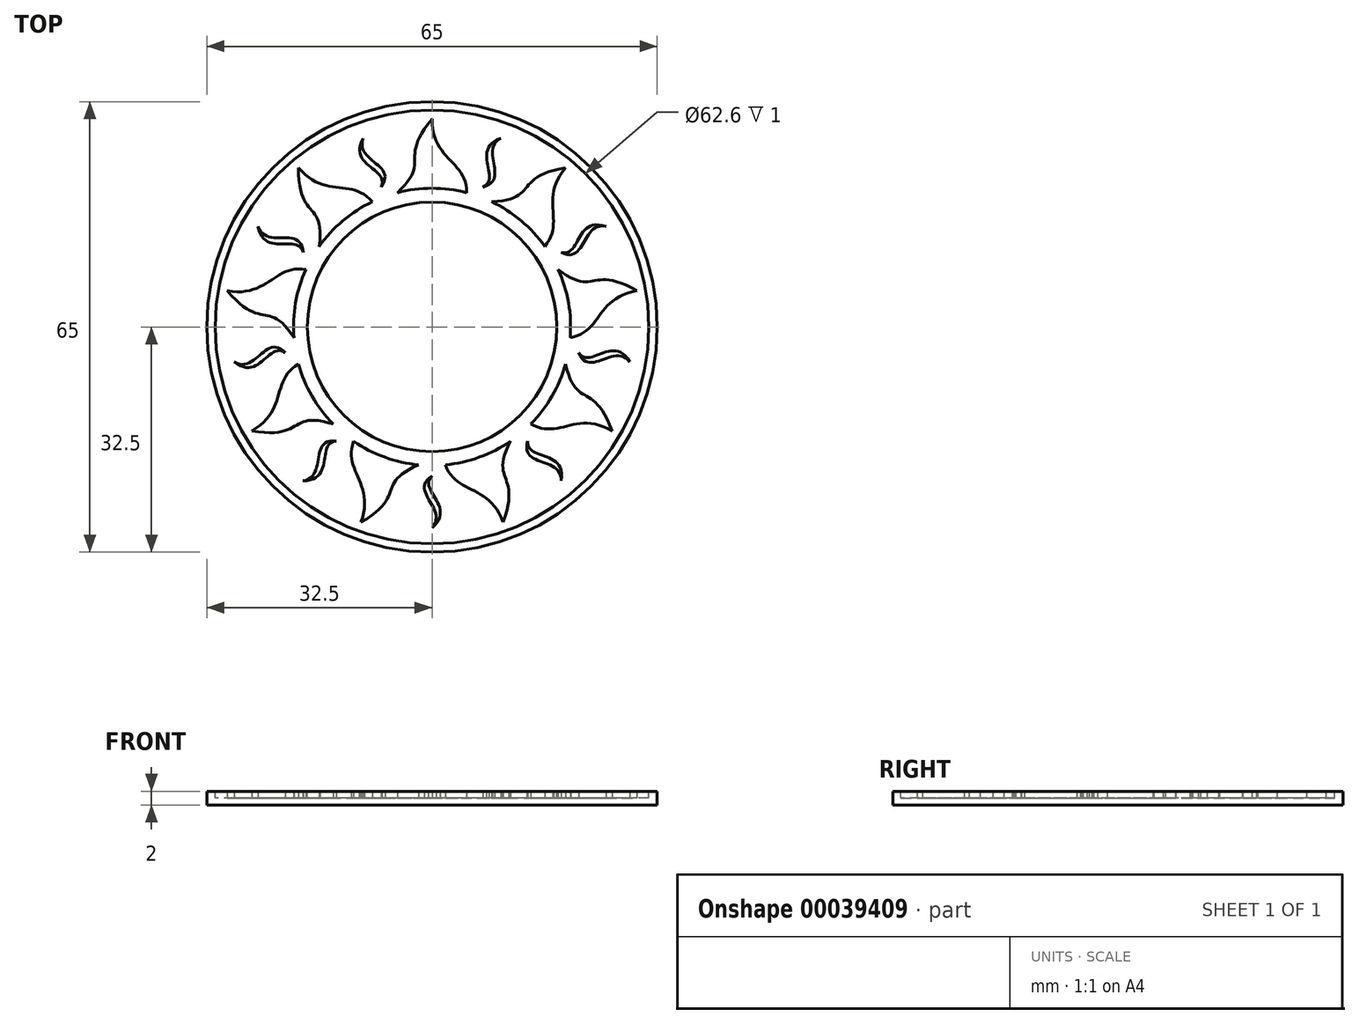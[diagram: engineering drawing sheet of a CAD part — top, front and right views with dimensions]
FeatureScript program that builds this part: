
annotation { "Feature Type Name" : "Feature", "Feature Type Description" : "" }
export const myFeature = defineFeature(function(context is Context, id is Id, definition is map)
    precondition{}
    {
        {
            var Q0;
            Q0=qCreatedBy(makeId("Top.planeOp"),FACE);
            var sketch = newSketch(context, id + "F0", { "sketchPlane" : qUnion([Q0])});
            skCircle(sketch, "E0", {"center": v(0, 0) * mm, "radius": 32.5 * mm});
            skSolve(sketch);
        }
        {
            var Q0;
            Q0=qSketchRegion(id+"F0",true);
            extrude(context, id + "F1", {"entities" : qUnion([Q0]), "depth" : 2 * mm});
        }
        {
            var Q0;
            Q0=makeQuery(id+"F1.opExtrude","CAP_FACE",FACE,{"disambiguationData":[OSD([sQuery(id+"F0.wireOp",EDGE,"E0")])],"isStart":false});
            var sketch = newSketch(context, id + "F2", { "sketchPlane" : qUnion([Q0])});
            skCircle(sketch, "E1", {"center": v(0, 0) * mm, "radius": 31.3 * mm});
            skCircle(sketch, "E2", {"center": v(0, 0) * mm, "radius": 18 * mm});
            skSolve(sketch);
        }
        {
            var Q0;
            Q0=qSketchRegion(id+"F2",true);
            extrude(context, id + "F3", {"entities" : qUnion([Q0]), "operationType" : NewBodyOperationType.REMOVE, "oppositeDirection" : true, "depth" : 1 * mm});
        }
        {
            var Q0;
            Q0=makeQuery(id+"F3.boolean.opBoolean","COPY",FACE,{"derivedFrom":makeQuery(id+"F3.opExtrude","CAP_FACE",FACE,{"disambiguationData":[OSD([sQuery(id+"F2.wireOp",EDGE,"E1"),sQuery(id+"F2.wireOp",EDGE,"E2")])],"isStart":false})});
            var sketch = newSketch(context, id + "F4", { "sketchPlane" : qUnion([Q0])});
            skArc(sketch, "E3", {"start": v(5, 19.36) * mm, "mid": v(0, 20) * mm, "end": v(-5, 19.36) * mm});
            skFitSpline(sketch, "E4", {"points": [v(-5, 19.36) * mm, v(0, 30) * mm], "startDerivative": vector(15, 13.9) * mm, "endDerivative": vector(15, 18) * mm});
            skFitSpline(sketch, "E5", {"points": [v(0, 30) * mm, v(5, 19.36) * mm], "startDerivative": vector(0, -18) * mm, "endDerivative": vector(0, -13.9) * mm});
            skLineSegment(sketch, "E6", {"start": v(0, 0) * mm, "end": v(0, 18) * mm, "construction": true});
            skLineSegment(sketch, "E7", {"start": v(0, 0) * mm, "end": v(15.39, 42.28) * mm, "construction": true});
            skFitSpline(sketch, "E8", {"points": [v(9.91, 27.24) * mm, v(7.35, 20.2) * mm], "startDerivative": vector(-13.2, -5.03) * mm, "endDerivative": vector(-8.1, -3.8) * mm});
            skFitSpline(sketch, "E9", {"points": [v(9.91, 27.24) * mm, v(7.35, 20.2) * mm], "startDerivative": vector(-9.54, -5.23) * mm, "endDerivative": vector(-11.92, -2.86) * mm});
            skSolve(sketch);
        }
        {
            var Q0;
            Q0 = qSketchRegion(id + "F4", true);
            var Q1;
            Q1=makeQuery(id+"F3.boolean.opBoolean","SPLIT",FACE,{"disambiguationData":[TD([makeQuery(id+"F3.opExtrude","SWEPT_FACE",FACE,{"disambiguationData":[OSD([sQuery(id+"F2.wireOp",EDGE,"E2")])]})])],"derivedFrom":makeQuery(id+"F1.opExtrude","CAP_FACE",FACE,{"disambiguationData":[OSD([sQuery(id+"F0.wireOp",EDGE,"E0")])],"isStart":false})});
            extrude(context, id + "F5", {"entities" : qUnion([Q0]), "operationType" : NewBodyOperationType.ADD, "endBound" : BoundingType.UP_TO_SURFACE, "endBoundEntityFace" : qUnion([Q1]), "depth" : 25 * mm});
        }
        {
            var Q0;
            Q0=makeQuery(id+"F1.opExtrude","SWEPT_BODY",BODY,{"disambiguationData":[OSD([sQuery(id+"F0.wireOp",EDGE,"E0")])]});
            var Q1;
            Q1=makeQuery(id+"F1.opExtrude","SWEPT_FACE",FACE,{"disambiguationData":[OSD([sQuery(id+"F0.wireOp",EDGE,"E0")])]});
            circularPattern(context, id + "F6", {"operationType" : NewBodyOperationType.ADD, "entities" : qUnion([Q0]), "axis" : qUnion([Q1]), "angle" : 360 * degree, "instanceCount" : 9, "equalSpace" : true});
        }
    });
